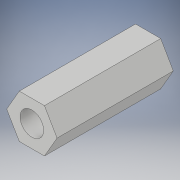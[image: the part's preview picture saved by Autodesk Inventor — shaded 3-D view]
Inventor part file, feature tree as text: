
AUTODESK INVENTOR PART (.ipt)
format: ipt  version: 2018 (Build 220112000, 112)  size: 96,768 bytes
history: native  units: in
note: dims shown in document units (in); Inventor stores cm internally (conversion verified against a paired STEP export)
features: extrude x1, sketch x1
ambient origin geometry x8: Origin, YZ Plane, XZ Plane, XY Plane, X Axis, Y Axis, Z Axis, Center Point
bodies: Solid1 (feature_tree)
feature tree (2):
  extrude  "Extrusion1"  Depth=1.0in
  sketch  "Sketch1"  dims[d0=0.375in d1=0.2031in d2=1.0in d3=0.0in]
